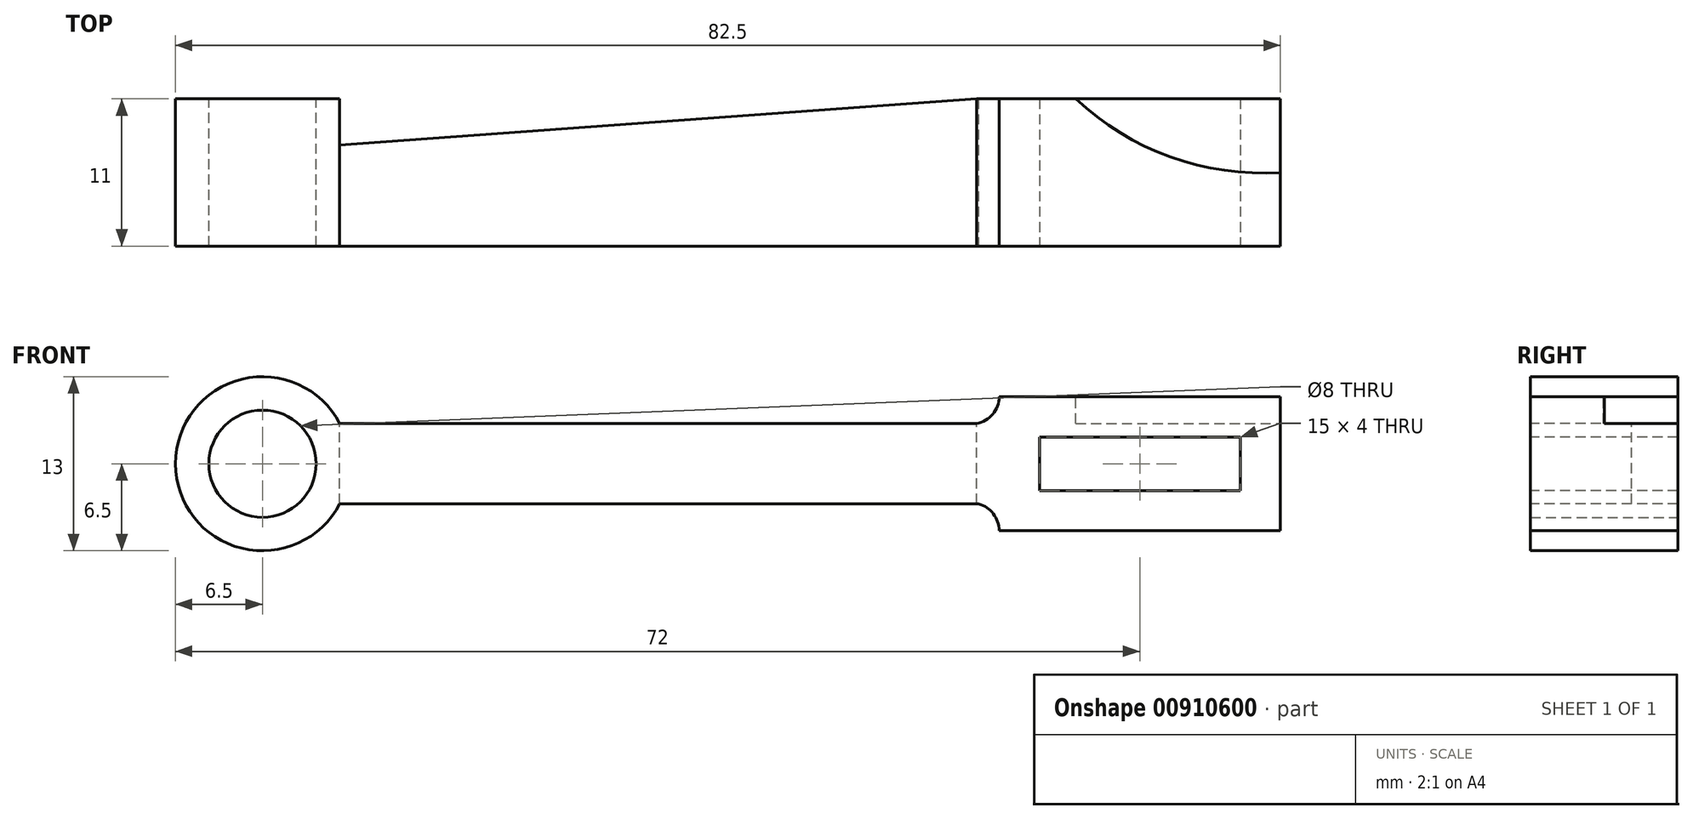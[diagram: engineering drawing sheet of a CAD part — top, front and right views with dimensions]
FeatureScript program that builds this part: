
annotation { "Feature Type Name" : "Feature", "Feature Type Description" : "" }
export const myFeature = defineFeature(function(context is Context, id is Id, definition is map)
    precondition{}
    {
        {
            var Q0;
            Q0=qCreatedBy(makeId("Front.planeOp"),FACE);
            var sketch = newSketch(context, id + "F0", { "sketchPlane" : qUnion([Q0])});
            skCircle(sketch, "E0", {"center": v(0, 0) * mm, "radius": 6.5 * mm});
            skCircle(sketch, "E1", {"center": v(0, 0) * mm, "radius": 4 * mm});
            skSolve(sketch);
        }
        {
            var Q0;
            Q0=makeQuery(id+"F0.imprint","IMPRINT",FACE,{"disambiguationData":[TD([[makeQuery(id+"F0.imprint","IMPRINT",EDGE,{"derivedFrom":sQuery(id+"F0.wireOp",EDGE,"E0")}),1.0]])]});
            var Q1;
            Q1=sQuery(id+"F0.wireOp",EDGE,"E0");
            extrude(context, id + "F1", {"entities" : qUnion([Q0]), "surfaceEntities" : qUnion([Q1]), "depth" : 15 * mm, "offsetDistance" : 25 * mm});
        }
        {
            var Q0;
            Q0=makeQuery(id+"F1.opExtrude","CAP_FACE",FACE,{"disambiguationData":[OSD([sQuery(id+"F0.wireOp",EDGE,"E0"),sQuery(id+"F0.wireOp",EDGE,"E1")])],"isStart":false});
            var sketch = newSketch(context, id + "F2", { "sketchPlane" : qUnion([Q0])});
            skLineSegment(sketch, "E2", {"start": v(0, 0) * mm, "end": v(0, 3) * mm});
            skLineSegment(sketch, "E3", {"start": v(0, 3) * mm, "end": v(55, 3) * mm});
            skLineSegment(sketch, "E4", {"start": v(55, 3) * mm, "end": v(55, -3) * mm});
            skLineSegment(sketch, "E5", {"start": v(55, -3) * mm, "end": v(0, -3) * mm});
            skSolve(sketch);
        }
        {
            var Q0;
            {var subQ0=sQuery(id+"F2.wireOp",EDGE,"E4");Q0=makeQuery(id+"F2.imprint","IMPRINT",FACE,{"disambiguationData":[TD([[makeQuery(id+"F2.imprint","IMPRINT",EDGE,{"derivedFrom":subQ0}),-1.0]])]});}
            extrude(context, id + "F3", {"entities" : qUnion([Q0]), "operationType" : NewBodyOperationType.ADD, "oppositeDirection" : true, "depth" : 15 * mm, "offsetDistance" : 25 * mm});
        }
        {
            var Q0;
            {var subQ0=sQuery(id+"F0.wireOp",EDGE,"E0");Q0=makeQuery(id+"F3.boolean.opBoolean","MERGE",FACE,{"derivedFrom":[makeQuery(id+"F1.opExtrude","CAP_FACE",FACE,{"disambiguationData":[OSD([subQ0,sQuery(id+"F0.wireOp",EDGE,"E1")])],"isStart":false}),makeQuery(id+"F3.opExtrude","CAP_FACE",FACE,{"disambiguationData":[OSD([subQ0,sQuery(id+"F2.wireOp",EDGE,"E3"),sQuery(id+"F2.wireOp",EDGE,"E4"),sQuery(id+"F2.wireOp",EDGE,"E5")])],"isStart":true})]});}
            var sketch = newSketch(context, id + "F4", { "sketchPlane" : qUnion([Q0])});
            skLineSegment(sketch, "E6", {"start": v(55, 0) * mm, "end": v(55, -2) * mm});
            skLineSegment(sketch, "E7", {"start": v(58, -2) * mm, "end": v(58, 2) * mm});
            skLineSegment(sketch, "E8", {"start": v(58, 2) * mm, "end": v(73, 2) * mm});
            skLineSegment(sketch, "E9", {"start": v(73, 2) * mm, "end": v(73, -2) * mm});
            skLineSegment(sketch, "E10", {"start": v(73, -2) * mm, "end": v(58, -2) * mm});
            skLineSegment(sketch, "E11", {"start": v(55, 3) * mm, "end": v(55, 5) * mm});
            skLineSegment(sketch, "E12", {"start": v(55, 5) * mm, "end": v(76, 5) * mm});
            skLineSegment(sketch, "E13", {"start": v(55, -3) * mm, "end": v(55, -5) * mm});
            skLineSegment(sketch, "E14", {"start": v(55, -5) * mm, "end": v(76, -5) * mm});
            skLineSegment(sketch, "E15", {"start": v(76, -5) * mm, "end": v(76, 5) * mm});
            skSolve(sketch);
        }
        {
            var Q0;
            {var subQ2=sQuery(id+"F4.wireOp",EDGE,"E6");Q0=makeQuery(id+"F4.imprint","IMPRINT",FACE,{"disambiguationData":[TD([[makeQuery(id+"F4.imprint","IMPRINT",EDGE,{"derivedFrom":subQ2}),1.0]])]});}
            extrude(context, id + "F5", {"entities" : qUnion([Q0]), "operationType" : NewBodyOperationType.ADD, "oppositeDirection" : true, "depth" : 15 * mm, "offsetDistance" : 25 * mm});
        }
        {
            var Q0;
            {var subQ0=sQuery(id+"F2.wireOp",EDGE,"E4");var subQ1=sQuery(id+"F0.wireOp",EDGE,"E0");Q0=makeQuery(id+"F5.boolean.opBoolean","MERGE",FACE,{"derivedFrom":[makeQuery(id+"F3.boolean.opBoolean","MERGE",FACE,{"derivedFrom":[makeQuery(id+"F1.opExtrude","CAP_FACE",FACE,{"disambiguationData":[OSD([subQ1,sQuery(id+"F0.wireOp",EDGE,"E1")])],"isStart":false}),makeQuery(id+"F3.opExtrude","CAP_FACE",FACE,{"disambiguationData":[OSD([subQ1,sQuery(id+"F2.wireOp",EDGE,"E3"),subQ0,sQuery(id+"F2.wireOp",EDGE,"E5")])],"isStart":true})]}),makeQuery(id+"F5.opExtrude","CAP_FACE",FACE,{"disambiguationData":[OSD([subQ0,sQuery(id+"F4.wireOp",EDGE,"E6"),sQuery(id+"F4.wireOp",EDGE,"E7"),sQuery(id+"F4.wireOp",EDGE,"E8"),sQuery(id+"F4.wireOp",EDGE,"E9"),sQuery(id+"F4.wireOp",EDGE,"E10"),sQuery(id+"F4.wireOp",EDGE,"E11"),sQuery(id+"F4.wireOp",EDGE,"E12"),sQuery(id+"F4.wireOp",EDGE,"E13"),sQuery(id+"F4.wireOp",EDGE,"E14"),sQuery(id+"F4.wireOp",EDGE,"E15")])],"isStart":true})]});}
            var sketch = newSketch(context, id + "F6", { "sketchPlane" : qUnion([Q0])});
            skArc(sketch, "E16", {"start": v(52.63, 3) * mm, "mid": v(54.28, 3.45) * mm, "end": v(55, 5) * mm});
            skLineSegment(sketch, "E17", {"start": v(55, 5) * mm, "end": v(55, 3) * mm});
            skLineSegment(sketch, "E18", {"start": v(55, 3) * mm, "end": v(52.63, 3) * mm});
            skArc(sketch, "E19", {"start": v(55, -5) * mm, "mid": v(54.2, -3.36) * mm, "end": v(52.4, -3) * mm});
            skLineSegment(sketch, "E20", {"start": v(55, -5) * mm, "end": v(55, -3) * mm});
            skLineSegment(sketch, "E21", {"start": v(55, -3) * mm, "end": v(52.4, -3) * mm});
            skSolve(sketch);
        }
        {
            var Q0;
            Q0 = qSketchRegion(id + "F6", true);
            extrude(context, id + "F7", {"entities" : qUnion([Q0]), "operationType" : NewBodyOperationType.ADD, "oppositeDirection" : true, "depth" : 15 * mm, "offsetDistance" : 25 * mm});
        }
        {
            var Q0;
            {var subQ0=sQuery(id+"F2.wireOp",EDGE,"E4");var subQ1=sQuery(id+"F0.wireOp",EDGE,"E0");Q0=makeQuery(id+"F7.boolean.opBoolean","MERGE",FACE,{"derivedFrom":[makeQuery(id+"F5.boolean.opBoolean","MERGE",FACE,{"derivedFrom":[makeQuery(id+"F3.boolean.opBoolean","MERGE",FACE,{"derivedFrom":[makeQuery(id+"F1.opExtrude","CAP_FACE",FACE,{"disambiguationData":[OSD([subQ1,sQuery(id+"F0.wireOp",EDGE,"E1")])],"isStart":false}),makeQuery(id+"F3.opExtrude","CAP_FACE",FACE,{"disambiguationData":[OSD([subQ1,sQuery(id+"F2.wireOp",EDGE,"E3"),subQ0,sQuery(id+"F2.wireOp",EDGE,"E5")])],"isStart":true})]}),makeQuery(id+"F5.opExtrude","CAP_FACE",FACE,{"disambiguationData":[OSD([subQ0,sQuery(id+"F4.wireOp",EDGE,"E6"),sQuery(id+"F4.wireOp",EDGE,"E7"),sQuery(id+"F4.wireOp",EDGE,"E8"),sQuery(id+"F4.wireOp",EDGE,"E9"),sQuery(id+"F4.wireOp",EDGE,"E10"),sQuery(id+"F4.wireOp",EDGE,"E11"),sQuery(id+"F4.wireOp",EDGE,"E12"),sQuery(id+"F4.wireOp",EDGE,"E13"),sQuery(id+"F4.wireOp",EDGE,"E14"),sQuery(id+"F4.wireOp",EDGE,"E15")])],"isStart":true})]}),makeQuery(id+"F7.opExtrude","CAP_FACE",FACE,{"disambiguationData":[OSD([sQuery(id+"F6.wireOp",EDGE,"E16"),sQuery(id+"F6.wireOp",EDGE,"E17"),sQuery(id+"F6.wireOp",EDGE,"E18")])],"isStart":true}),makeQuery(id+"F7.opExtrude","CAP_FACE",FACE,{"disambiguationData":[OSD([sQuery(id+"F6.wireOp",EDGE,"E19"),sQuery(id+"F6.wireOp",EDGE,"E20"),sQuery(id+"F6.wireOp",EDGE,"E21")])],"isStart":true})]});}
            extrude(context, id + "F8", {"entities" : qUnion([Q0]), "operationType" : NewBodyOperationType.REMOVE, "oppositeDirection" : true, "depth" : 4 * mm, "offsetDistance" : 25 * mm});
        }
        {
            var Q0;
            Q0=makeQuery(id+"F5.opExtrude","SWEPT_FACE",FACE,{"disambiguationData":[OSD([sQuery(id+"F4.wireOp",EDGE,"E12")])]});
            var sketch = newSketch(context, id + "F9", { "sketchPlane" : qUnion([Q0])});
            skArc(sketch, "E22", {"start": v(60.71, 0) * mm, "mid": v(67.79, -4.33) * mm, "end": v(76, -5.5) * mm});
            skSolve(sketch);
        }
        {
            var Q0;
            {var subQ0=sQuery(id+"F9.wireOp",EDGE,"E22");Q0=makeQuery(id+"F9.imprint","IMPRINT",FACE,{"disambiguationData":[TD([[makeQuery(id+"F9.imprint","IMPRINT",EDGE,{"derivedFrom":subQ0}),1.0]])]});}
            extrude(context, id + "F10", {"entities" : qUnion([Q0]), "operationType" : NewBodyOperationType.REMOVE, "oppositeDirection" : true, "depth" : 2 * mm, "offsetDistance" : 25 * mm});
        }
        {
            var Q0;
            Q0=makeQuery(id+"F3.opExtrude","SWEPT_FACE",FACE,{"disambiguationData":[OSD([sQuery(id+"F2.wireOp",EDGE,"E3")])]});
            var sketch = newSketch(context, id + "F11", { "sketchPlane" : qUnion([Q0])});
            skLineSegment(sketch, "E23", {"start": v(5.77, -3.45) * mm, "end": v(53.31, 0) * mm});
            skSolve(sketch);
        }
        {
            var Q0;
            {var subQ0=sQuery(id+"F11.wireOp",EDGE,"E23");Q0=makeQuery(id+"F11.imprint","IMPRINT",FACE,{"disambiguationData":[TD([[makeQuery(id+"F11.imprint","IMPRINT",EDGE,{"derivedFrom":subQ0}),1.0]])]});}
            extrude(context, id + "F12", {"entities" : qUnion([Q0]), "operationType" : NewBodyOperationType.REMOVE, "oppositeDirection" : true, "depth" : 25 * mm, "offsetDistance" : 25 * mm});
        }
    });
